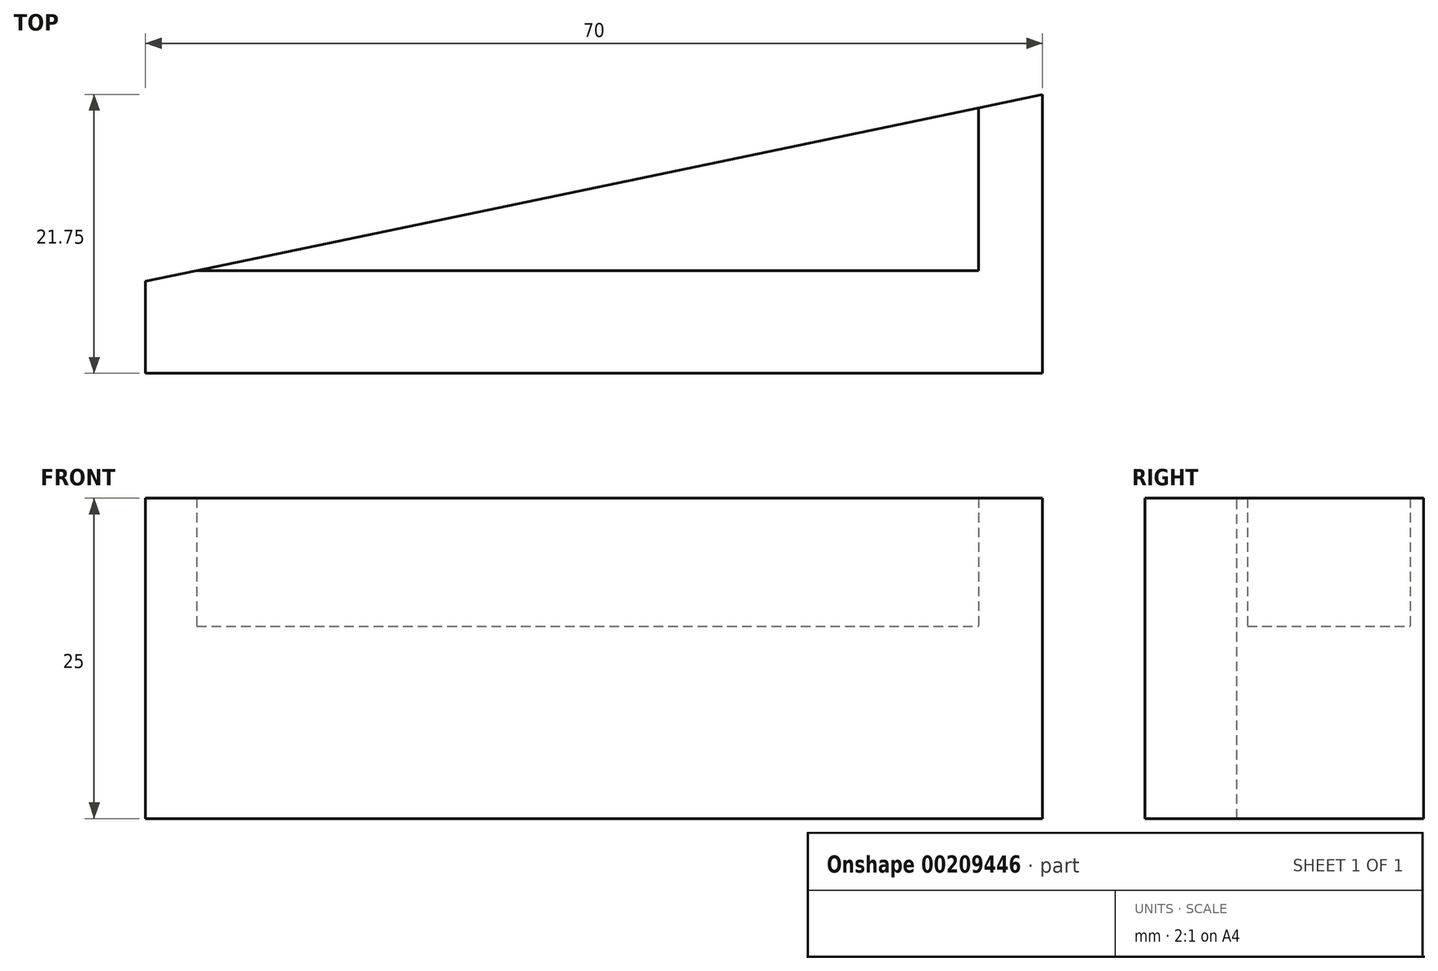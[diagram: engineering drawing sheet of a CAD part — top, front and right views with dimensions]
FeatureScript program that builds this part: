
annotation { "Feature Type Name" : "Feature", "Feature Type Description" : "" }
export const myFeature = defineFeature(function(context is Context, id is Id, definition is map)
    precondition{}
    {
        {
            var Q0;
            Q0=qCreatedBy(makeId("Top.planeOp"),FACE);
            var sketch = newSketch(context, id + "F0", { "sketchPlane" : qUnion([Q0])});
            skLineSegment(sketch, "E0", {"start": v(0, 0) * mm, "end": v(60, 0) * mm});
            skLineSegment(sketch, "E1", {"start": v(60, 0) * mm, "end": v(90, 0) * mm});
            skLineSegment(sketch, "E2", {"start": v(90, 0) * mm, "end": v(90, 18.75) * mm});
            skLineSegment(sketch, "E3", {"start": v(60, 0) * mm, "end": v(60, 12.5) * mm});
            skLineSegment(sketch, "E4", {"start": v(0, 0) * mm, "end": v(90, 18.75) * mm});
            skSolve(sketch);
        }
        {
            var Q0;
            Q0 = qSketchRegion(id + "F0", true);
            extrude(context, id + "F1", {"entities" : qUnion([Q0]), "depth" : 15 * mm});
        }
        {
            var Q0;
            Q0=makeQuery(id+"F1.opExtrude","CAP_FACE",FACE,{"disambiguationData":[OSD([sQuery(id+"F0.wireOp",EDGE,"E0"),sQuery(id+"F0.wireOp",EDGE,"HZKhCLW9-oDJk-jZ79-Cc5a-FlSk4M4CYGuW"),sQuery(id+"F0.wireOp",EDGE,"E1"),sQuery(id+"F0.wireOp",EDGE,"E2")])],"isStart":false});
            var sketch = newSketch(context, id + "F2", { "sketchPlane" : qUnion([Q0])});
            skLineSegment(sketch, "E5", {"start": v(90, 0) * mm, "end": v(90, 0) * mm});
            skLineSegment(sketch, "E6", {"start": v(90, 0) * mm, "end": v(0, 0) * mm});
            skLineSegment(sketch, "E7", {"start": v(90, 0) * mm, "end": v(90, 18.75) * mm});
            skLineSegment(sketch, "E8", {"start": v(90, 18.75) * mm, "end": v(85, 17.7) * mm});
            skLineSegment(sketch, "E9.0", {"start": v(85, 5) * mm, "end": v(85, 17.7) * mm});
            skLineSegment(sketch, "E10.0", {"start": v(85, 5) * mm, "end": v(24, 5) * mm});
            skLineSegment(sketch, "E11.trimOffspring", {"start": v(24, 5) * mm, "end": v(0, 0) * mm});
            skSolve(sketch);
        }
        {
            var Q0;
            Q0 = qSketchRegion(id + "F2", true);
            extrude(context, id + "F3", {"entities" : qUnion([Q0]), "operationType" : NewBodyOperationType.ADD, "depth" : 10 * mm});
        }
        {
            var Q0;
            Q0=makeQuery(id+"F3.boolean.opBoolean","MERGE",FACE,{"derivedFrom":[makeQuery(id+"F1.opExtrude","SWEPT_FACE",FACE,{"disambiguationData":[OSD([sQuery(id+"F0.wireOp",EDGE,"E0"),sQuery(id+"F0.wireOp",EDGE,"E1")])]}),makeQuery(id+"F3.opExtrude","SWEPT_FACE",FACE,{"disambiguationData":[OSD([sQuery(id+"F2.wireOp",EDGE,"E6")])]})]});
            extrude(context, id + "F4", {"entities" : qUnion([Q0]), "operationType" : NewBodyOperationType.ADD, "depth" : 3 * mm});
        }
        {
            var Q0;
            {var subQ0=sQuery(id+"F2.wireOp",EDGE,"E6");Q0=makeQuery(id+"F4.boolean.opBoolean","MERGE",FACE,{"derivedFrom":[makeQuery(id+"F3.opExtrude","CAP_FACE",FACE,{"disambiguationData":[OSD([subQ0,sQuery(id+"F2.wireOp",EDGE,"E7"),sQuery(id+"F2.wireOp",EDGE,"E8"),sQuery(id+"F2.wireOp",EDGE,"E9.0"),sQuery(id+"F2.wireOp",EDGE,"E10.0"),sQuery(id+"F2.wireOp",EDGE,"E11.trimOffspring")])],"isStart":false}),makeQuery(id+"F4.opExtrude","SWEPT_FACE",FACE,{"disambiguationData":[OSD([subQ0])]})]});}
            var sketch = newSketch(context, id + "F5", { "sketchPlane" : qUnion([Q0])});
            skLineSegment(sketch, "E12.0", {"start": v(20, -3) * mm, "end": v(20, 4.17) * mm});
            skLineSegment(sketch, "E13.0", {"start": v(0, 0) * mm, "end": v(20, 4.17) * mm});
            skPoint(sketch, "E14.0", {"position": v(0, 0) * mm});
            skLineSegment(sketch, "E15.0", {"start": v(0, -3) * mm, "end": v(0, 0) * mm});
            skPoint(sketch, "E16.orphan", {"position": v(24, 5) * mm});
            skLineSegment(sketch, "E17", {"start": v(0, -3) * mm, "end": v(20, -3) * mm});
            skSolve(sketch);
        }
        {
            var Q0;
            Q0 = qSketchRegion(id + "F5", true);
            extrude(context, id + "F6", {"entities" : qUnion([Q0]), "operationType" : NewBodyOperationType.REMOVE, "endBound" : BoundingType.UP_TO_NEXT, "oppositeDirection" : true, "depth" : 25 * mm});
        }
    });
